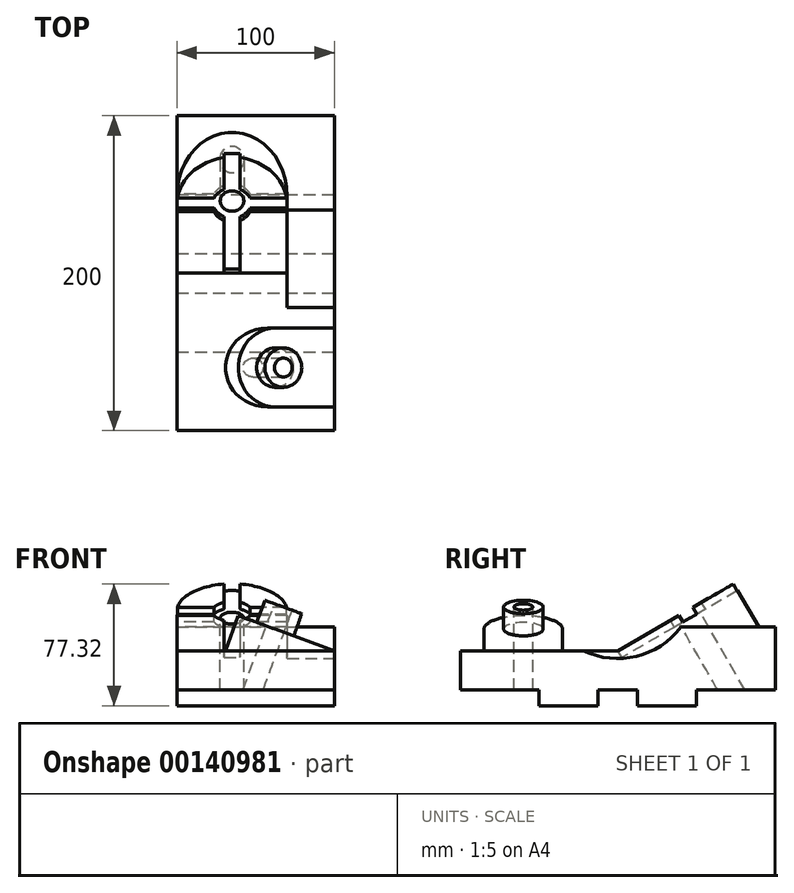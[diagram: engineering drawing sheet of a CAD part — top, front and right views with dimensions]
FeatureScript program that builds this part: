
annotation { "Feature Type Name" : "Feature", "Feature Type Description" : "" }
export const myFeature = defineFeature(function(context is Context, id is Id, definition is map)
    precondition{}
    {
        {
            var Q0;
            Q0=qCreatedBy(makeId("Right.planeOp"),FACE);
            var sketch = newSketch(context, id + "F0", { "sketchPlane" : qUnion([Q0])});
            skLineSegment(sketch, "E0", {"start": v(0, 0) * mm, "end": v(50, 0) * mm});
            skLineSegment(sketch, "E1", {"start": v(50, 0) * mm, "end": v(50, -10) * mm});
            skLineSegment(sketch, "E2", {"start": v(50, -10) * mm, "end": v(87.5, -10) * mm});
            skLineSegment(sketch, "E3", {"start": v(87.5, -10) * mm, "end": v(87.5, 0) * mm});
            skLineSegment(sketch, "E4", {"start": v(87.5, 0) * mm, "end": v(112.5, 0) * mm});
            skLineSegment(sketch, "E5", {"start": v(112.5, 0) * mm, "end": v(112.5, -10) * mm});
            skLineSegment(sketch, "E6", {"start": v(112.5, -10) * mm, "end": v(150, -10) * mm});
            skLineSegment(sketch, "E7", {"start": v(150, -10) * mm, "end": v(150, 0) * mm});
            skLineSegment(sketch, "E8", {"start": v(150, 0) * mm, "end": v(200, 0) * mm});
            skLineSegment(sketch, "E9", {"start": v(200, 0) * mm, "end": v(200, 40) * mm});
            skLineSegment(sketch, "E10", {"start": v(200, 40) * mm, "end": v(140, 40) * mm});
            skLineSegment(sketch, "E11", {"start": v(140, 40) * mm, "end": v(100, 25) * mm});
            skLineSegment(sketch, "E12", {"start": v(100, 25) * mm, "end": v(0, 25) * mm});
            skLineSegment(sketch, "E13", {"start": v(0, 25) * mm, "end": v(0, 0) * mm});
            skSolve(sketch);
        }
        {
            var Q0;
            Q0=makeQuery(id+"F0.imprint","IMPRINT",FACE,{"disambiguationData":[TD([[makeQuery(id+"F0.imprint","IMPRINT",EDGE,{"derivedFrom":sQuery(id+"F0.wireOp",EDGE,"E0")}),1.0]])]});
            extrude(context, id + "F1", {"entities" : qUnion([Q0]), "oppositeDirection" : true, "depth" : 100 * mm});
        }
        {
            var Q0;
            Q0=makeQuery(id+"F1.opExtrude","SWEPT_EDGE",EDGE,{"disambiguationData":[OSD([sQuery(id+"F0.wireOp",EDGE,"E11"),sQuery(id+"F0.wireOp",EDGE,"E12")])]});
            cPlane(context, id + "F2", {"entities" : qUnion([Q0]), "cplaneType" : CPlaneType.LINE_ANGLE, "offset" : 25 * mm, "angle" : 120 * degree, "width" : 150 * mm, "height" : 150 * mm});
        }
        {
            var Q0;
            Q0=qCreatedBy(id+"F2.planeOp",FACE);
            var sketch = newSketch(context, id + "F3", { "sketchPlane" : qUnion([Q0])});
            skLineSegment(sketch, "E14.0", {"start": v(0, 141.24) * mm, "end": v(0, 99.1) * mm});
            skLineSegment(sketch, "E15.0", {"start": v(-100, 149.1) * mm, "end": v(-100, 99.1) * mm});
            skLineSegment(sketch, "E16.0", {"start": v(-100, 99.1) * mm, "end": v(-30, 99.1) * mm});
            skLineSegment(sketch, "E17.0", {"start": v(-30, 149.1) * mm, "end": v(-30, 99.1) * mm});
            skArc(sketch, "E18", {"start": v(-100, 149.1) * mm, "mid": v(-65, 184.1) * mm, "end": v(-30, 149.1) * mm});
            skSolve(sketch);
        }
        {
            var Q0;
            Q0=makeQuery(id+"F3.imprint","IMPRINT",FACE,{"disambiguationData":[TD([[makeQuery(id+"F3.imprint","IMPRINT",EDGE,{"derivedFrom":sQuery(id+"F3.wireOp",EDGE,"E15.0")}),1.0]])]});
            var Q1;
            Q1=makeQuery(id+"F1.opExtrude","SWEPT_FACE",FACE,{"disambiguationData":[OSD([sQuery(id+"F0.wireOp",EDGE,"E11")])]});
            var Q2;
            Q2=makeQuery(id+"F1.opExtrude","SWEPT_BODY",BODY,{"disambiguationData":[OSD([sQuery(id+"F0.wireOp",EDGE,"E0"),sQuery(id+"F0.wireOp",EDGE,"E1"),sQuery(id+"F0.wireOp",EDGE,"E2"),sQuery(id+"F0.wireOp",EDGE,"E3"),sQuery(id+"F0.wireOp",EDGE,"E4"),sQuery(id+"F0.wireOp",EDGE,"E5"),sQuery(id+"F0.wireOp",EDGE,"E6"),sQuery(id+"F0.wireOp",EDGE,"E7"),sQuery(id+"F0.wireOp",EDGE,"E8"),sQuery(id+"F0.wireOp",EDGE,"E9"),sQuery(id+"F0.wireOp",EDGE,"E10"),sQuery(id+"F0.wireOp",EDGE,"E11"),sQuery(id+"F0.wireOp",EDGE,"E12"),sQuery(id+"F0.wireOp",EDGE,"E13")])]});
            extrude(context, id + "F4", {"entities" : qUnion([Q0]), "operationType" : NewBodyOperationType.ADD, "endBound" : BoundingType.UP_TO_BODY, "oppositeDirection" : true, "endBoundEntityFace" : qUnion([Q1]), "endBoundEntityBody" : qUnion([Q2]), "depth" : 25 * mm});
        }
        {
            var Q0;
            Q0=makeQuery(id+"F1.opExtrude","CAP_FACE",FACE,{"disambiguationData":[OSD([sQuery(id+"F0.wireOp",EDGE,"E0"),sQuery(id+"F0.wireOp",EDGE,"E1"),sQuery(id+"F0.wireOp",EDGE,"E2"),sQuery(id+"F0.wireOp",EDGE,"E3"),sQuery(id+"F0.wireOp",EDGE,"E4"),sQuery(id+"F0.wireOp",EDGE,"E5"),sQuery(id+"F0.wireOp",EDGE,"E6"),sQuery(id+"F0.wireOp",EDGE,"E7"),sQuery(id+"F0.wireOp",EDGE,"E8"),sQuery(id+"F0.wireOp",EDGE,"E9"),sQuery(id+"F0.wireOp",EDGE,"E10"),sQuery(id+"F0.wireOp",EDGE,"E11"),sQuery(id+"F0.wireOp",EDGE,"E12"),sQuery(id+"F0.wireOp",EDGE,"E13")])],"isStart":true});
            var sketch = newSketch(context, id + "F5", { "sketchPlane" : qUnion([Q0])});
            skArc(sketch, "E19", {"start": v(78.2, 25) * mm, "mid": v(111.8, 21.41) * mm, "end": v(140, 40) * mm});
            skLineSegment(sketch, "E20.0", {"start": v(100, 25) * mm, "end": v(78.2, 25) * mm});
            skLineSegment(sketch, "E21.0", {"start": v(140, 40) * mm, "end": v(100, 25) * mm});
            skPoint(sketch, "E22.orphan", {"position": v(0, 25) * mm});
            skSolve(sketch);
        }
        {
            var Q0;
            Q0=makeQuery(id+"F5.imprint","IMPRINT",FACE,{"disambiguationData":[TD([[makeQuery(id+"F5.imprint","IMPRINT",EDGE,{"derivedFrom":sQuery(id+"F5.wireOp",EDGE,"E19")}),1.0]])]});
            var Q1;
            Q1=makeQuery(id+"F4.opExtrude","SWEPT_FACE",FACE,{"disambiguationData":[OSD([sQuery(id+"F3.wireOp",EDGE,"E17.0")])]});
            extrude(context, id + "F6", {"entities" : qUnion([Q0]), "operationType" : NewBodyOperationType.REMOVE, "endBound" : BoundingType.UP_TO_SURFACE, "oppositeDirection" : true, "endBoundEntityFace" : qUnion([Q1]), "depth" : 25 * mm});
        }
        {
            var Q0;
            Q0=makeQuery(id+"F1.opExtrude","CAP_EDGE",EDGE,{"disambiguationData":[OSD([sQuery(id+"F0.wireOp",EDGE,"E12")])],"isStart":true});
            cPlane(context, id + "F7", {"entities" : qUnion([Q0]), "cplaneType" : CPlaneType.LINE_ANGLE, "offset" : 25 * mm, "angle" : 160 * degree, "width" : 150 * mm, "height" : 150 * mm});
        }
        {
            var Q0;
            Q0=qCreatedBy(id+"F7.planeOp",FACE);
            var sketch = newSketch(context, id + "F8", { "sketchPlane" : qUnion([Q0])});
            skLineSegment(sketch, "E23", {"start": v(-8.55, 15) * mm, "end": v(-8.55, 65) * mm});
            skLineSegment(sketch, "E24", {"start": v(-8.55, 65) * mm, "end": v(-48.55, 65) * mm});
            skLineSegment(sketch, "E25", {"start": v(-8.55, 15) * mm, "end": v(-48.55, 15) * mm});
            skArc(sketch, "E26", {"start": v(-48.55, 65) * mm, "mid": v(-73.55, 40) * mm, "end": v(-48.55, 15) * mm});
            skSolve(sketch);
        }
        {
            var Q0;
            Q0=makeQuery(id+"F8.imprint","IMPRINT",FACE,{"disambiguationData":[TD([[makeQuery(id+"F8.imprint","IMPRINT",EDGE,{"derivedFrom":sQuery(id+"F8.wireOp",EDGE,"E23")}),1.0]])]});
            var Q1;
            Q1=makeQuery(id+"F1.opExtrude","SWEPT_BODY",BODY,{"disambiguationData":[OSD([sQuery(id+"F0.wireOp",EDGE,"E0"),sQuery(id+"F0.wireOp",EDGE,"E1"),sQuery(id+"F0.wireOp",EDGE,"E2"),sQuery(id+"F0.wireOp",EDGE,"E3"),sQuery(id+"F0.wireOp",EDGE,"E4"),sQuery(id+"F0.wireOp",EDGE,"E5"),sQuery(id+"F0.wireOp",EDGE,"E6"),sQuery(id+"F0.wireOp",EDGE,"E7"),sQuery(id+"F0.wireOp",EDGE,"E8"),sQuery(id+"F0.wireOp",EDGE,"E9"),sQuery(id+"F0.wireOp",EDGE,"E10"),sQuery(id+"F0.wireOp",EDGE,"E11"),sQuery(id+"F0.wireOp",EDGE,"E12"),sQuery(id+"F0.wireOp",EDGE,"E13")])]});
            extrude(context, id + "F9", {"entities" : qUnion([Q0]), "operationType" : NewBodyOperationType.ADD, "endBound" : BoundingType.UP_TO_BODY, "oppositeDirection" : true, "endBoundEntityBody" : qUnion([Q1]), "depth" : 25 * mm});
        }
        {
            var Q0;
            Q0=makeQuery(id+"F9.opExtrude","CAP_FACE",FACE,{"disambiguationData":[OSD([sQuery(id+"F8.wireOp",EDGE,"E23"),sQuery(id+"F8.wireOp",EDGE,"E24"),sQuery(id+"F8.wireOp",EDGE,"E25"),sQuery(id+"F8.wireOp",EDGE,"E26")])],"isStart":true});
            var sketch = newSketch(context, id + "F10", { "sketchPlane" : qUnion([Q0])});
            skCircle(sketch, "E27", {"center": v(-48.55, 40) * mm, "radius": 12.5 * mm});
            skSolve(sketch);
        }
        {
            var Q0;
            Q0=makeQuery(id+"F10.imprint","IMPRINT",FACE,{"disambiguationData":[TD([[makeQuery(id+"F10.imprint","IMPRINT",EDGE,{"derivedFrom":sQuery(id+"F10.wireOp",EDGE,"E27")}),1.0]])]});
            extrude(context, id + "F11", {"entities" : qUnion([Q0]), "operationType" : NewBodyOperationType.ADD, "depth" : 15 * mm});
        }
        {
            var Q0;
            Q0=makeQuery(id+"F11.opExtrude","CAP_FACE",FACE,{"disambiguationData":[OSD([sQuery(id+"F10.wireOp",EDGE,"E27")])],"isStart":false});
            var sketch = newSketch(context, id + "F12", { "sketchPlane" : qUnion([Q0])});
            skCircle(sketch, "E28", {"center": v(-48.55, 40) * mm, "radius": 6 * mm});
            skSolve(sketch);
        }
        {
            var Q0;
            Q0=makeQuery(id+"F12.imprint","IMPRINT",FACE,{"disambiguationData":[TD([[makeQuery(id+"F12.imprint","IMPRINT",EDGE,{"derivedFrom":sQuery(id+"F12.wireOp",EDGE,"E28")}),1.0]])]});
            extrude(context, id + "F13", {"entities" : qUnion([Q0]), "operationType" : NewBodyOperationType.REMOVE, "endBound" : BoundingType.THROUGH_ALL, "oppositeDirection" : true, "depth" : 25 * mm});
        }
        {
            var Q0;
            Q0=makeQuery(id+"F4.opExtrude","CAP_FACE",FACE,{"disambiguationData":[OSD([sQuery(id+"F3.wireOp",EDGE,"E15.0"),sQuery(id+"F3.wireOp",EDGE,"E16.0"),sQuery(id+"F3.wireOp",EDGE,"E17.0"),sQuery(id+"F3.wireOp",EDGE,"E18")])],"isStart":true});
            var sketch = newSketch(context, id + "F14", { "sketchPlane" : qUnion([Q0])});
            skLineSegment(sketch, "E29", {"start": v(-30, 149.1) * mm, "end": v(-100, 149.1) * mm, "construction": true});
            skLineSegment(sketch, "E30", {"start": v(-65, 184.1) * mm, "end": v(-65, 99.1) * mm, "construction": true});
            skLineSegment(sketch, "E31.0", {"start": v(-70, 183.74) * mm, "end": v(-70, 160.56) * mm});
            skLineSegment(sketch, "E32.0", {"start": v(-60, 183.74) * mm, "end": v(-60, 160.56) * mm});
            skLineSegment(sketch, "E33.0", {"start": v(-30.36, 154.1) * mm, "end": v(-53.54, 154.1) * mm});
            skLineSegment(sketch, "E34.0", {"start": v(-30, 144.1) * mm, "end": v(-53.54, 144.1) * mm});
            skArc(sketch, "E35", {"start": v(-53.54, 154.1) * mm, "mid": v(-56.16, 157.94) * mm, "end": v(-60, 160.56) * mm});
            skArc(sketch, "E36.0", {"start": v(-100, 149.1) * mm, "mid": v(-99.91, 151.6) * mm, "end": v(-99.64, 154.1) * mm});
            skLineSegment(sketch, "E37.0", {"start": v(-100, 149.1) * mm, "end": v(-100, 144.1) * mm});
            skLineSegment(sketch, "E38.0", {"start": v(-70, 99.1) * mm, "end": v(-60, 99.1) * mm});
            skLineSegment(sketch, "E39.0", {"start": v(-30, 149.1) * mm, "end": v(-30, 144.1) * mm});
            skPoint(sketch, "E40.orphan", {"position": v(-30, 99.1) * mm});
            skArc(sketch, "E41.trimOffspring", {"start": v(-30.36, 154.1) * mm, "mid": v(-30.09, 151.6) * mm, "end": v(-30, 149.1) * mm});
            skArc(sketch, "E42.trimOffspring", {"start": v(-70, 183.74) * mm, "mid": v(-65, 184.1) * mm, "end": v(-60, 183.74) * mm});
            skPoint(sketch, "E43.orphan", {"position": v(-100, 99.1) * mm});
            skLineSegment(sketch, "E44.trimOffspring", {"start": v(-60, 137.65) * mm, "end": v(-60, 99.1) * mm});
            skLineSegment(sketch, "E45.trimOffspring", {"start": v(-70, 137.65) * mm, "end": v(-70, 99.1) * mm});
            skLineSegment(sketch, "E46.trimOffspring", {"start": v(-76.46, 144.1) * mm, "end": v(-100, 144.1) * mm});
            skLineSegment(sketch, "E47.trimOffspring", {"start": v(-76.46, 154.1) * mm, "end": v(-99.64, 154.1) * mm});
            skArc(sketch, "E48.trimOffspring", {"start": v(-76.46, 144.1) * mm, "mid": v(-73.84, 140.26) * mm, "end": v(-70, 137.65) * mm});
            skArc(sketch, "E49.trimOffspring", {"start": v(-70, 160.56) * mm, "mid": v(-73.84, 157.94) * mm, "end": v(-76.46, 154.1) * mm});
            skArc(sketch, "E50.trimOffspring", {"start": v(-60, 137.65) * mm, "mid": v(-56.16, 140.26) * mm, "end": v(-53.54, 144.1) * mm});
            skSolve(sketch);
        }
        {
            var Q0;
            Q0=makeQuery(id+"F14.imprint","IMPRINT",FACE,{"disambiguationData":[TD([[makeQuery(id+"F14.imprint","IMPRINT",EDGE,{"derivedFrom":sQuery(id+"F14.wireOp",EDGE,"E31.0")}),1.0]])]});
            extrude(context, id + "F15", {"entities" : qUnion([Q0]), "operationType" : NewBodyOperationType.REMOVE, "oppositeDirection" : true, "depth" : 5 * mm});
        }
        {
            var Q0;
            Q0=makeQuery(id+"F15.boolean.opBoolean","COPY",FACE,{"derivedFrom":makeQuery(id+"F15.opExtrude","CAP_FACE",FACE,{"disambiguationData":[OSD([sQuery(id+"F14.wireOp",EDGE,"E31.0"),sQuery(id+"F14.wireOp",EDGE,"E32.0"),sQuery(id+"F14.wireOp",EDGE,"E33.0"),sQuery(id+"F14.wireOp",EDGE,"E34.0"),sQuery(id+"F14.wireOp",EDGE,"E35"),sQuery(id+"F14.wireOp",EDGE,"E36.0"),sQuery(id+"F14.wireOp",EDGE,"E37.0"),sQuery(id+"F14.wireOp",EDGE,"E38.0"),sQuery(id+"F14.wireOp",EDGE,"E39.0"),sQuery(id+"F14.wireOp",EDGE,"E41.trimOffspring"),sQuery(id+"F14.wireOp",EDGE,"E42.trimOffspring"),sQuery(id+"F14.wireOp",EDGE,"E44.trimOffspring"),sQuery(id+"F14.wireOp",EDGE,"E45.trimOffspring"),sQuery(id+"F14.wireOp",EDGE,"E46.trimOffspring"),sQuery(id+"F14.wireOp",EDGE,"E47.trimOffspring"),sQuery(id+"F14.wireOp",EDGE,"E48.trimOffspring"),sQuery(id+"F14.wireOp",EDGE,"E49.trimOffspring"),sQuery(id+"F14.wireOp",EDGE,"E50.trimOffspring")])],"isStart":false})});
            var sketch = newSketch(context, id + "F16", { "sketchPlane" : qUnion([Q0])});
            skCircle(sketch, "E51", {"center": v(-65, 149.1) * mm, "radius": 7.5 * mm});
            skSolve(sketch);
        }
        {
            var Q0;
            Q0=makeQuery(id+"F16.imprint","IMPRINT",FACE,{"disambiguationData":[TD([[makeQuery(id+"F16.imprint","IMPRINT",EDGE,{"derivedFrom":sQuery(id+"F16.wireOp",EDGE,"E51")}),1.0]])]});
            extrude(context, id + "F17", {"entities" : qUnion([Q0]), "operationType" : NewBodyOperationType.REMOVE, "endBound" : BoundingType.THROUGH_ALL, "oppositeDirection" : true, "depth" : 25 * mm});
        }
    });
